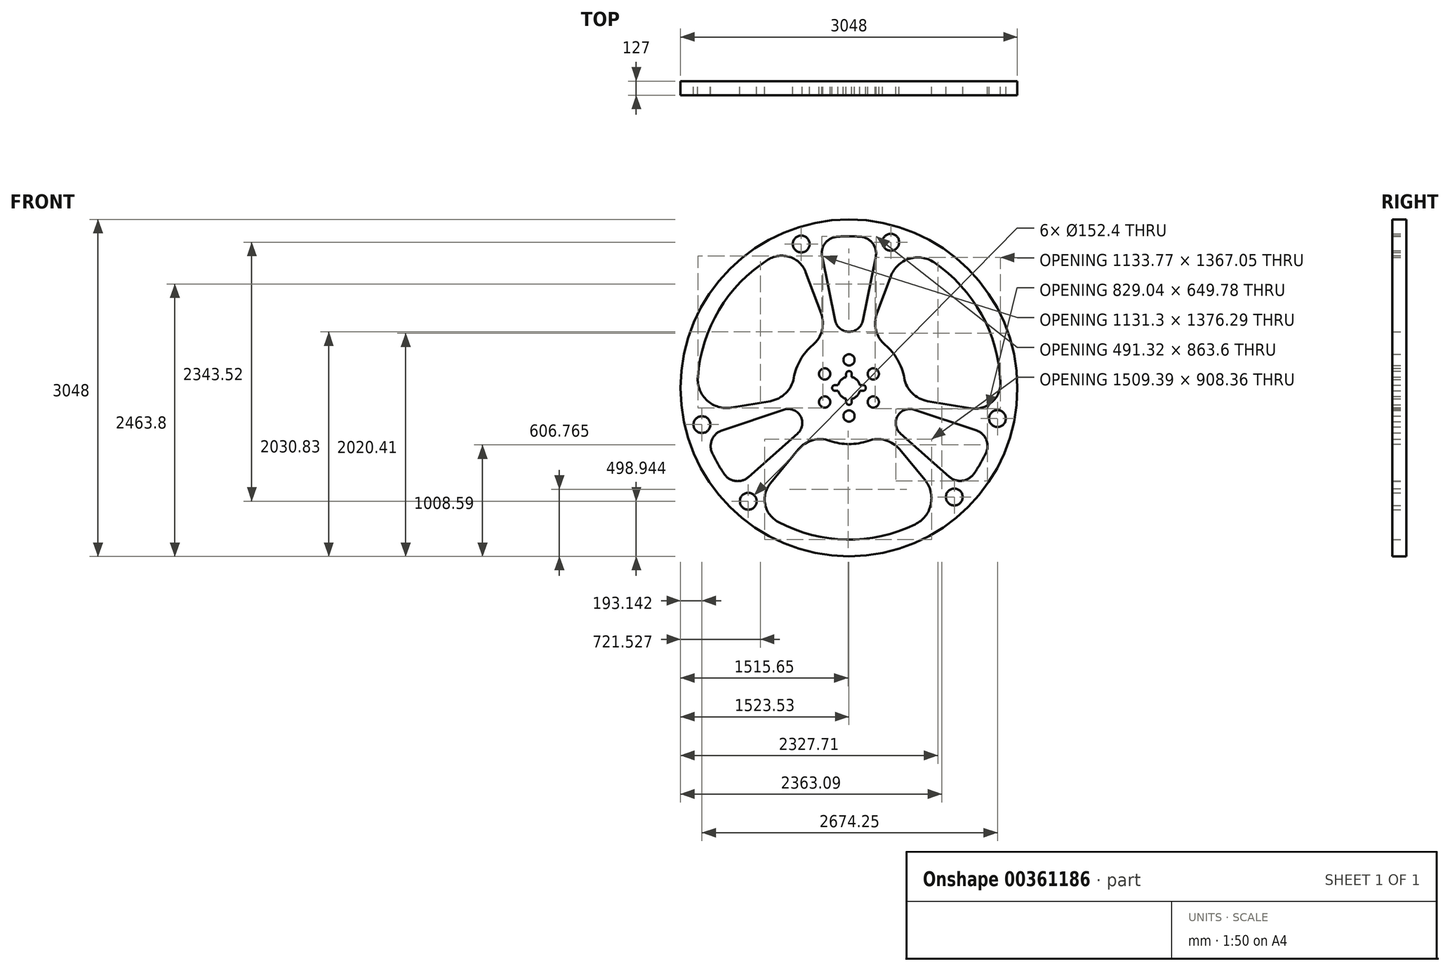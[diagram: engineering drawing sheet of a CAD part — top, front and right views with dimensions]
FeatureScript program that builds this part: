
annotation { "Feature Type Name" : "Feature", "Feature Type Description" : "" }
export const myFeature = defineFeature(function(context is Context, id is Id, definition is map)
    precondition{}
    {
        {
            var Q0;
            Q0=qCreatedBy(makeId("Front.planeOp"),FACE);
            var sketch = newSketch(context, id + "F0", { "sketchPlane" : qUnion([Q0])});
            skCircle(sketch, "E0", {"center": v(0, 0) * mm, "radius": 1524 * mm});
            skArc(sketch, "E1", {"start": v(105.38, 1367.55) * mm, "mid": v(-2.87, 1371.6) * mm, "end": v(-111.1, 1367.1) * mm});
            skLineSegment(sketch, "E2", {"start": v(124.43, 609.6) * mm, "end": v(242.14, 1186.24) * mm});
            skLineSegment(sketch, "E3", {"start": v(-124.43, 609.6) * mm, "end": v(-243.16, 1191.25) * mm});
            skArc(sketch, "E4", {"start": v(242.14, 1186.24) * mm, "mid": v(214.66, 1307.74) * mm, "end": v(105.38, 1367.55) * mm});
            skArc(sketch, "E5", {"start": v(-111.1, 1367.1) * mm, "mid": v(-216.68, 1308.88) * mm, "end": v(-243.16, 1191.25) * mm});
            skArc(sketch, "E6.trimOffspring", {"start": v(-503.68, 1275.77) * mm, "mid": v(-1356.7, 201.69) * mm, "end": v(-853.01, -1074.09) * mm});
            skArc(sketch, "E7", {"start": v(-124.43, 609.6) * mm, "mid": v(0, 508) * mm, "end": v(124.43, 609.6) * mm});
            skArc(sketch, "E8.1.0", {"start": v(-1148.38, -383.42) * mm, "mid": v(-1239.87, -467.97) * mm, "end": v(-1237.02, -592.52) * mm});
            skLineSegment(sketch, "E8.1.1", {"start": v(-590.15, -197.04) * mm, "end": v(-1148.38, -383.42) * mm});
            skArc(sketch, "E8.1.2", {"start": v(-1237.02, -592.52) * mm, "mid": v(-1186.4, -688.28) * mm, "end": v(-1128.4, -779.76) * mm});
            skArc(sketch, "E8.1.3", {"start": v(-1128.4, -779.76) * mm, "mid": v(-1025.18, -842.1) * mm, "end": v(-910.07, -806.2) * mm});
            skLineSegment(sketch, "E8.1.4", {"start": v(-465.71, -412.56) * mm, "end": v(-910.07, -806.2) * mm});
            skArc(sketch, "E8.1.5", {"start": v(-465.71, -412.56) * mm, "mid": v(-439.94, -254) * mm, "end": v(-590.15, -197.04) * mm});
            skArc(sketch, "E8.2.0", {"start": v(906.24, -802.82) * mm, "mid": v(1025.21, -839.77) * mm, "end": v(1131.64, -775.03) * mm});
            skLineSegment(sketch, "E8.2.1", {"start": v(465.71, -412.56) * mm, "end": v(906.24, -802.82) * mm});
            skArc(sketch, "E8.2.2", {"start": v(1131.64, -775.03) * mm, "mid": v(1189.27, -683.31) * mm, "end": v(1239.48, -587.34) * mm});
            skArc(sketch, "E8.2.3", {"start": v(1239.48, -587.34) * mm, "mid": v(1241.87, -466.79) * mm, "end": v(1153.23, -385.04) * mm});
            skLineSegment(sketch, "E8.2.4", {"start": v(590.15, -197.04) * mm, "end": v(1153.23, -385.04) * mm});
            skArc(sketch, "E8.2.5", {"start": v(590.15, -197.04) * mm, "mid": v(439.94, -254) * mm, "end": v(465.71, -412.56) * mm});
            skLineSegment(sketch, "E9", {"start": v(0, 508) * mm, "end": v(0, 508) * mm});
            skLineSegment(sketch, "E10", {"start": v(-459.34, -557.22) * mm, "end": v(-710.3, -861.67) * mm});
            skArc(sketch, "E11", {"start": v(499.9, 90.4) * mm, "mid": v(439.94, 254) * mm, "end": v(328.23, 387.72) * mm});
            skArc(sketch, "E12", {"start": v(459.34, -557.22) * mm, "mid": v(328.02, -472.14) * mm, "end": v(171.66, -478.12) * mm});
            skArc(sketch, "E13", {"start": v(-171.66, -478.12) * mm, "mid": v(-328.02, -472.14) * mm, "end": v(-459.34, -557.22) * mm});
            skArc(sketch, "E14", {"start": v(-710.3, -861.67) * mm, "mid": v(-758.59, -1054.24) * mm, "end": v(-639.74, -1213.27) * mm});
            skCircle(sketch, "E15", {"center": v(378.06, 1318.47) * mm, "radius": 76.2 * mm});
            skCircle(sketch, "E16", {"center": v(-432.05, 1301.77) * mm, "radius": 76.2 * mm});
            skCircle(sketch, "E17.1.0", {"center": v(-1330.86, -331.82) * mm, "radius": 76.2 * mm});
            skCircle(sketch, "E17.1.1", {"center": v(-911.34, -1025.06) * mm, "radius": 76.2 * mm});
            skCircle(sketch, "E17.2.0", {"center": v(952.8, -986.65) * mm, "radius": 76.2 * mm});
            skCircle(sketch, "E17.2.1", {"center": v(1343.4, -276.72) * mm, "radius": 76.2 * mm});
            skArc(sketch, "E18.trimOffspring", {"start": v(599.56, -1233.62) * mm, "mid": v(740.39, -1054.56) * mm, "end": v(686.8, -833.16) * mm});
            skLineSegment(sketch, "E19.trimOffspring", {"start": v(459.34, -557.22) * mm, "end": v(686.8, -833.16) * mm});
            skArc(sketch, "E20.trimOffspring", {"start": v(872.44, -1058.36) * mm, "mid": v(1350.1, 241.9) * mm, "end": v(450.7, 1295.44) * mm});
            skArc(sketch, "E21.trimOffspring", {"start": v(-639.74, -1213.27) * mm, "mid": v(-22.52, -1371.42) * mm, "end": v(599.56, -1233.62) * mm});
            skArc(sketch, "E22.1.0", {"start": v(252.9, 676.4) * mm, "mid": v(244.88, 520.14) * mm, "end": v(328.23, 387.72) * mm});
            skLineSegment(sketch, "E22.1.1", {"start": v(252.9, 676.4) * mm, "end": v(378.13, 1011.36) * mm});
            skArc(sketch, "E22.1.2", {"start": v(768.56, 1136.04) * mm, "mid": v(543.09, 1168.47) * mm, "end": v(378.13, 1011.36) * mm});
            skArc(sketch, "E22.1.3", {"start": v(1370.6, 52.6) * mm, "mid": v(1198.94, 666.2) * mm, "end": v(768.56, 1136.04) * mm});
            skArc(sketch, "E22.1.4", {"start": v(1101.38, -184.3) * mm, "mid": v(1292.3, -129.84) * mm, "end": v(1370.6, 52.6) * mm});
            skLineSegment(sketch, "E22.1.5", {"start": v(712.24, -119.19) * mm, "end": v(1101.38, -184.3) * mm});
            skArc(sketch, "E22.1.6", {"start": v(499.9, 90.4) * mm, "mid": v(572.9, -48) * mm, "end": v(712.24, -119.19) * mm});
            skArc(sketch, "E22.2.0", {"start": v(-712.24, -119.19) * mm, "mid": v(-572.9, -48) * mm, "end": v(-499.9, 90.4) * mm});
            skLineSegment(sketch, "E22.2.1", {"start": v(-712.24, -119.19) * mm, "end": v(-1064.93, -178.2) * mm});
            skArc(sketch, "E22.2.2", {"start": v(-1368.12, 97.57) * mm, "mid": v(-1283.47, -113.91) * mm, "end": v(-1064.93, -178.2) * mm});
            skArc(sketch, "E22.2.3", {"start": v(-730.85, 1160.66) * mm, "mid": v(-1176.42, 705.2) * mm, "end": v(-1368.12, 97.57) * mm});
            skArc(sketch, "E22.2.4", {"start": v(-391.08, 1045.98) * mm, "mid": v(-533.7, 1184.08) * mm, "end": v(-730.85, 1160.66) * mm});
            skLineSegment(sketch, "E22.2.5", {"start": v(-252.9, 676.4) * mm, "end": v(-391.08, 1045.98) * mm});
            skArc(sketch, "E22.2.6", {"start": v(-328.23, 387.72) * mm, "mid": v(-244.88, 520.14) * mm, "end": v(-252.9, 676.4) * mm});
            skLineSegment(sketch, "E23.trimOffspring", {"start": v(378.06, 1318.47) * mm, "end": v(399.07, 1391.71) * mm});
            skArc(sketch, "E24.trimOffspring", {"start": v(-171.66, -478.12) * mm, "mid": v(0, -508) * mm, "end": v(171.66, -478.12) * mm});
            skArc(sketch, "E25.trimOffspring", {"start": v(-328.23, 387.72) * mm, "mid": v(-439.94, 254) * mm, "end": v(-499.9, 90.4) * mm});
            skLineSegment(sketch, "E26.trimOffspring", {"start": v(-242.12, 639.4) * mm, "end": v(-252.15, 674.4) * mm});
            skPoint(sketch, "E27.start.orphan", {"position": v(-58.78, 0) * mm});
            skCircle(sketch, "E28", {"center": v(0, 0) * mm, "radius": 381 * mm});
            skCircle(sketch, "E29", {"center": v(0, 254) * mm, "radius": 50.8 * mm});
            skCircle(sketch, "E30.1.0", {"center": v(-219.97, -127) * mm, "radius": 50.8 * mm});
            skCircle(sketch, "E30.2.0", {"center": v(219.97, -127) * mm, "radius": 50.8 * mm});
            skCircle(sketch, "E31", {"center": v(0, -254) * mm, "radius": 50.8 * mm});
            skCircle(sketch, "E32.1.0", {"center": v(219.97, 127) * mm, "radius": 50.8 * mm});
            skCircle(sketch, "E32.2.0", {"center": v(-219.97, 127) * mm, "radius": 50.8 * mm});
            skArc(sketch, "E33", {"start": v(-25.4, 98.37) * mm, "mid": v(-71.84, 71.84) * mm, "end": v(-98.37, 25.4) * mm});
            skArc(sketch, "E34", {"start": v(-25.4, -127) * mm, "mid": v(0, -152.4) * mm, "end": v(25.4, -127) * mm});
            skArc(sketch, "E35", {"start": v(127, -25.4) * mm, "mid": v(152.4, 0) * mm, "end": v(127, 25.4) * mm});
            skArc(sketch, "E36", {"start": v(25.4, 127) * mm, "mid": v(0, 152.4) * mm, "end": v(-25.4, 127) * mm});
            skArc(sketch, "E37", {"start": v(-127, 25.4) * mm, "mid": v(-152.4, 0) * mm, "end": v(-127, -25.4) * mm});
            skLineSegment(sketch, "E38", {"start": v(-25.4, -98.37) * mm, "end": v(-25.4, -127) * mm});
            skLineSegment(sketch, "E39", {"start": v(25.4, -98.37) * mm, "end": v(25.4, -127) * mm});
            skLineSegment(sketch, "E40", {"start": v(98.37, 25.4) * mm, "end": v(127, 25.4) * mm});
            skLineSegment(sketch, "E41", {"start": v(98.37, -25.4) * mm, "end": v(127, -25.4) * mm});
            skLineSegment(sketch, "E42", {"start": v(25.4, 98.37) * mm, "end": v(25.4, 127) * mm});
            skLineSegment(sketch, "E43", {"start": v(-25.4, 98.37) * mm, "end": v(-25.4, 127) * mm});
            skLineSegment(sketch, "E44", {"start": v(-98.37, 25.4) * mm, "end": v(-127, 25.4) * mm});
            skLineSegment(sketch, "E45", {"start": v(-98.37, -25.4) * mm, "end": v(-127, -25.4) * mm});
            skPoint(sketch, "E46.orphan", {"position": v(0, -508) * mm});
            skArc(sketch, "E47.trimOffspring", {"start": v(-98.37, -25.4) * mm, "mid": v(-71.84, -71.84) * mm, "end": v(-25.4, -98.37) * mm});
            skArc(sketch, "E48.trimOffspring", {"start": v(25.4, -98.37) * mm, "mid": v(71.84, -71.84) * mm, "end": v(98.37, -25.4) * mm});
            skArc(sketch, "E49.trimOffspring", {"start": v(98.37, 25.4) * mm, "mid": v(71.84, 71.84) * mm, "end": v(25.4, 98.37) * mm});
            skSolve(sketch);
        }
        {
            var Q0;
            Q0=makeQuery(id+"F0.imprint","IMPRINT",FACE,{"disambiguationData":[TD([[makeQuery(id+"F0.imprint","IMPRINT",EDGE,{"derivedFrom":sQuery(id+"F0.wireOp",EDGE,"E0")}),1.0]])]});
            var Q1;
            Q1=makeQuery(id+"F0.imprint","IMPRINT",FACE,{"disambiguationData":[TD([[makeQuery(id+"F0.imprint","IMPRINT",EDGE,{"derivedFrom":sQuery(id+"F0.wireOp",EDGE,"E28")}),1.0]])]});
            extrude(context, id + "F1", {"entities" : qUnion([Q0, Q1]), "depth" : 127 * mm});
        }
    });
